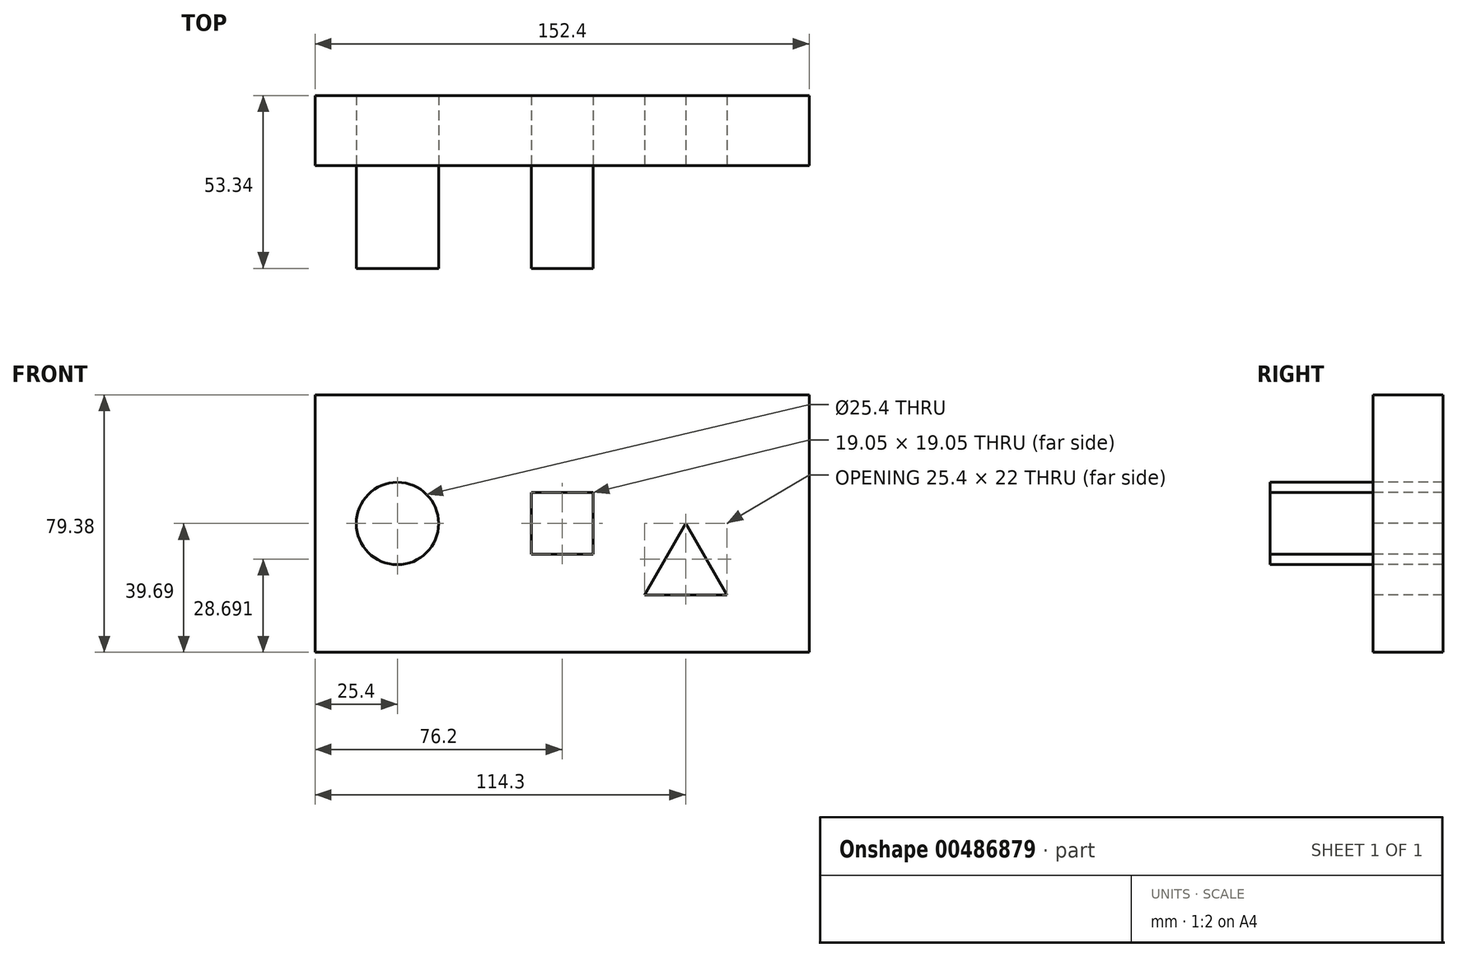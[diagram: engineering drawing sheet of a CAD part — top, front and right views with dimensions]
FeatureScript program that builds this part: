
annotation { "Feature Type Name" : "Feature", "Feature Type Description" : "" }
export const myFeature = defineFeature(function(context is Context, id is Id, definition is map)
    precondition{}
    {
        {
            var Q0;
            Q0=qCreatedBy(makeId("Front.planeOp"),FACE);
            var sketch = newSketch(context, id + "F0", { "sketchPlane" : qUnion([Q0])});
            skLineSegment(sketch, "E0", {"start": v(6.35, 0) * mm, "end": v(19.05, -22) * mm});
            skLineSegment(sketch, "E1", {"start": v(19.05, -22) * mm, "end": v(-6.35, -22) * mm});
            skLineSegment(sketch, "E2", {"start": v(-6.35, -22) * mm, "end": v(6.35, 0) * mm});
            skLineSegment(sketch, "E3.bottom", {"start": v(-22.22, 9.52) * mm, "end": v(-41.27, 9.52) * mm});
            skLineSegment(sketch, "E3.top", {"start": v(-22.22, -9.53) * mm, "end": v(-41.27, -9.53) * mm});
            skLineSegment(sketch, "E3.left", {"start": v(-22.22, 9.52) * mm, "end": v(-22.23, -9.53) * mm});
            skLineSegment(sketch, "E3.right", {"start": v(-41.27, 9.52) * mm, "end": v(-41.27, -9.53) * mm});
            skPoint(sketch, "E3.middle", {"position": v(-31.75, 0) * mm});
            skCircle(sketch, "E4", {"center": v(-82.55, 0) * mm, "radius": 12.7 * mm});
            skLineSegment(sketch, "E5.bottom", {"start": v(44.45, -39.69) * mm, "end": v(-107.95, -39.69) * mm});
            skLineSegment(sketch, "E5.top", {"start": v(44.45, 39.69) * mm, "end": v(-107.95, 39.69) * mm});
            skLineSegment(sketch, "E5.left", {"start": v(44.45, -39.69) * mm, "end": v(44.45, 39.69) * mm});
            skLineSegment(sketch, "E5.right", {"start": v(-107.95, -39.69) * mm, "end": v(-107.95, 39.69) * mm});
            skSolve(sketch);
        }
        {
            var Q0;
            Q0=makeQuery(id+"F0.imprint","IMPRINT",FACE,{"disambiguationData":[TD([[makeQuery(id+"F0.imprint","IMPRINT",EDGE,{"derivedFrom":sQuery(id+"F0.wireOp",EDGE,"E0")}),1.0]])]});
            extrude(context, id + "F1", {"entities" : qUnion([Q0]), "oppositeDirection" : true, "depth" : 21.59 * mm});
        }
        {
            var Q0;
            Q0=makeQuery(id+"F0.imprint","IMPRINT",FACE,{"disambiguationData":[TD([[makeQuery(id+"F0.imprint","IMPRINT",EDGE,{"derivedFrom":sQuery(id+"F0.wireOp",EDGE,"E4")}),1.0]])]});
            extrude(context, id + "F2", {"entities" : qUnion([Q0]), "operationType" : NewBodyOperationType.ADD, "depth" : 31.75 * mm});
        }
        {
            var Q0;
            Q0=makeQuery(id+"F0.imprint","IMPRINT",FACE,{"disambiguationData":[TD([[makeQuery(id+"F0.imprint","IMPRINT",EDGE,{"derivedFrom":sQuery(id+"F0.wireOp",EDGE,"E4")}),1.0]])]});
            extrude(context, id + "F3", {"entities" : qUnion([Q0]), "oppositeDirection" : true, "depth" : 21.59 * mm});
        }
        {
            var Q0;
            Q0=makeQuery(id+"F0.imprint","IMPRINT",FACE,{"disambiguationData":[TD([[makeQuery(id+"F0.imprint","IMPRINT",EDGE,{"derivedFrom":sQuery(id+"F0.wireOp",EDGE,"E3.bottom")}),1.0]])]});
            extrude(context, id + "F4", {"entities" : qUnion([Q0]), "depth" : 31.75 * mm});
        }
    });
